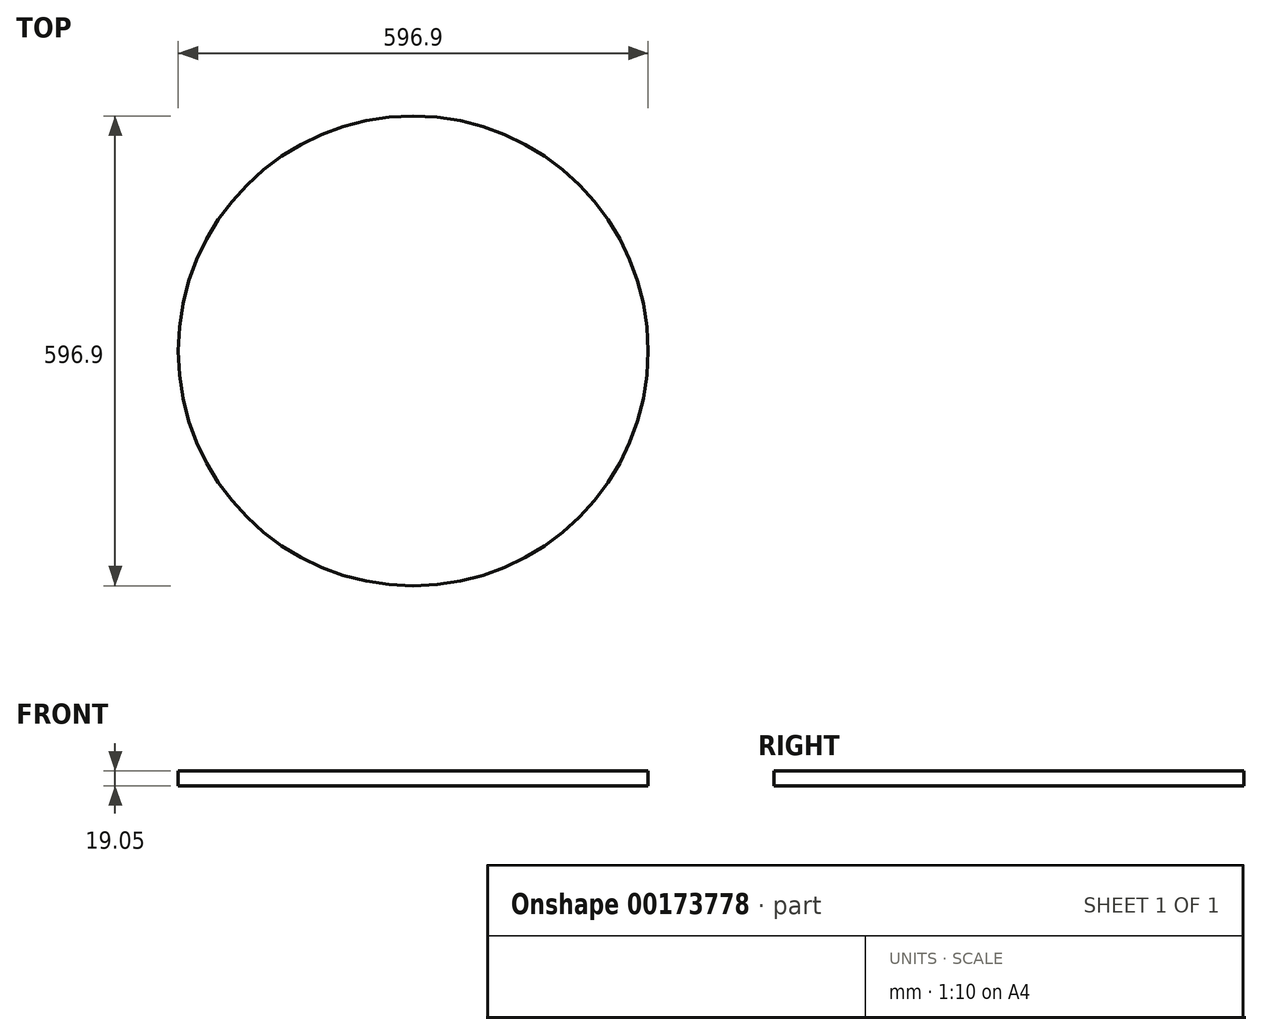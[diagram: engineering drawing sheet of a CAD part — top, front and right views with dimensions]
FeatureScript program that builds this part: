
annotation { "Feature Type Name" : "Feature", "Feature Type Description" : "" }
export const myFeature = defineFeature(function(context is Context, id is Id, definition is map)
    precondition{}
    {
        {
            var Q0;
            Q0=qCreatedBy(makeId("Top.planeOp"),FACE);
            var sketch = newSketch(context, id + "F0", { "sketchPlane" : qUnion([Q0])});
            skCircle(sketch, "E0", {"center": v(0, 0) * mm, "radius": 298.45 * mm});
            skSolve(sketch);
        }
        {
            var Q0;
            Q0=sQuery(id+"F0.wireOp",EDGE,"E0");
            extrude(context, id + "F1", {"bodyType" : ToolBodyType.SURFACE, "surfaceEntities" : qUnion([Q0]), "depth" : 19.05 * mm});
        }
    });
